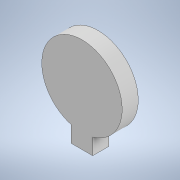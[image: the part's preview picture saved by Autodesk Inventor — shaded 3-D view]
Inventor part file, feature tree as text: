
AUTODESK INVENTOR PART (.ipt)
format: ipt  version: 2021 (Build 250183000, 183)  size: 95,232 bytes
history: native  units: mm
features: extrude x1, sketch x1
ambient origin geometry x8: Origin, YZ Plane, XZ Plane, XY Plane, X Axis, Y Axis, Z Axis, Center Point
bodies: Solid1 (feature_tree)
feature tree (2):
  extrude  "Extrusion1"  [1 undecoded]
  sketch  "Sketch1"  dims[d0=3.0mm d1=0.0mm]
note: 1 required parameter value undecoded (feature->parameter linkage not recoverable at this tier; creation-order binding heuristic only, values carry confidence <= 0.55)
